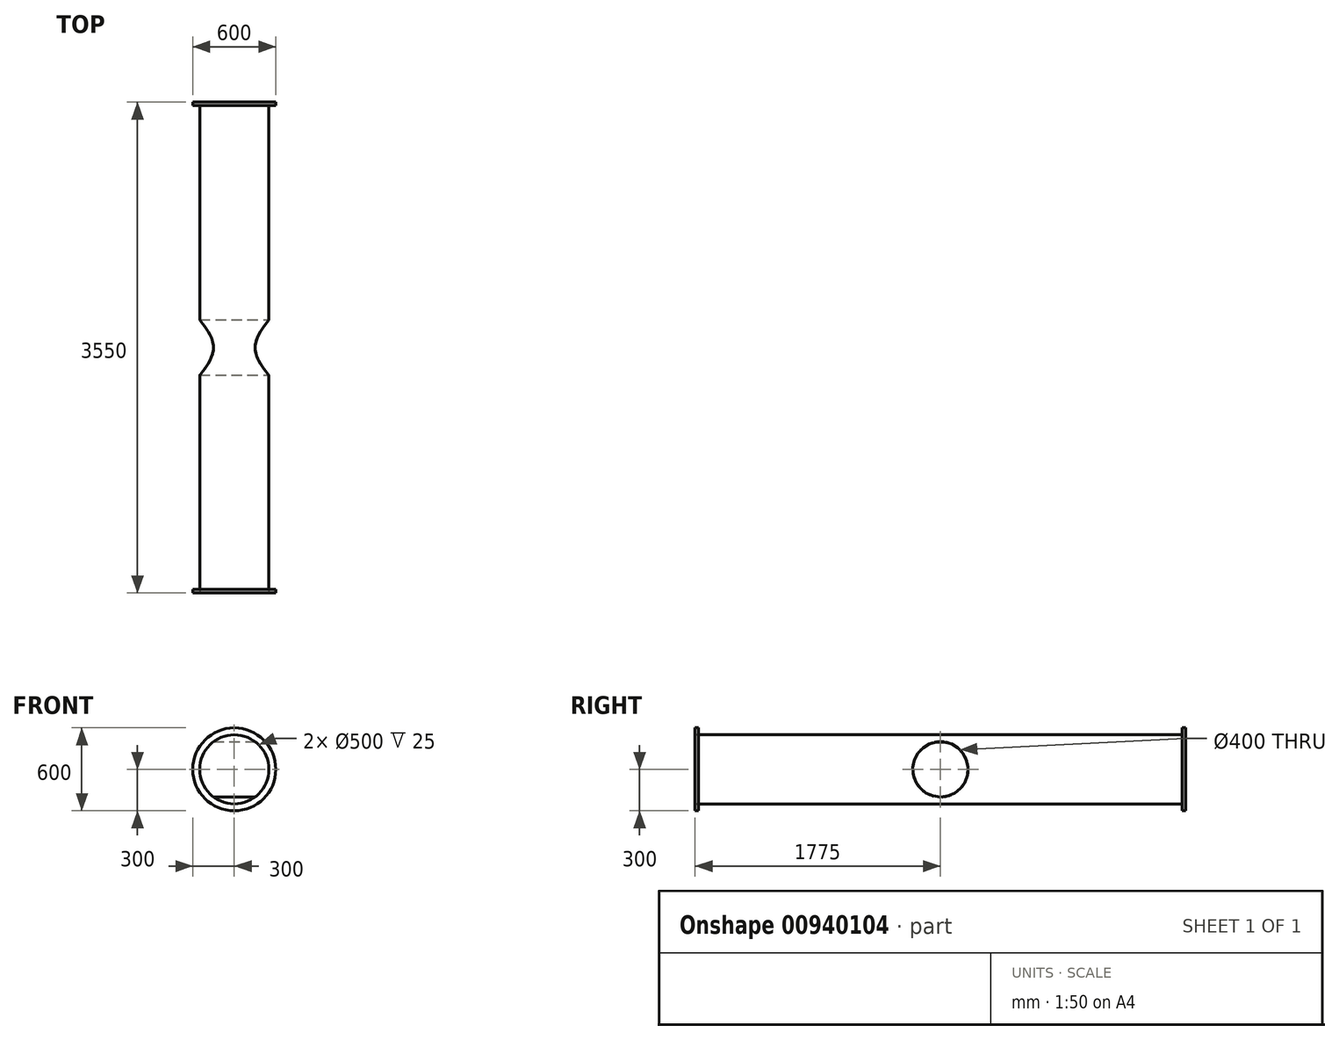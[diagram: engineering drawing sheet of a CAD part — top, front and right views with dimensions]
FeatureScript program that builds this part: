
annotation { "Feature Type Name" : "Feature", "Feature Type Description" : "" }
export const myFeature = defineFeature(function(context is Context, id is Id, definition is map)
    precondition{}
    {
        {
            var Q0;
            Q0=qCreatedBy(makeId("Front.planeOp"),FACE);
            var sketch = newSketch(context, id + "F0", { "sketchPlane" : qUnion([Q0])});
            skCircle(sketch, "E0", {"center": v(0, 0) * mm, "radius": 250 * mm});
            skSolve(sketch);
        }
        {
            var Q0;
            Q0=makeQuery(id+"F0.imprint","IMPRINT",FACE,{"disambiguationData":[TD([[makeQuery(id+"F0.imprint","IMPRINT",EDGE,{"derivedFrom":sQuery(id+"F0.wireOp",EDGE,"E0")}),1.0]])]});
            extrude(context, id + "F1", {"entities" : qUnion([Q0]), "endBound" : BoundingType.SYMMETRIC, "depth" : 3550 * mm, "offsetDistance" : 25 * mm});
        }
        {
            var Q0;
            Q0=makeQuery(id+"F1.opExtrude","CAP_FACE",FACE,{"disambiguationData":[OSD([sQuery(id+"F0.wireOp",EDGE,"E0")])],"isStart":false});
            var sketch = newSketch(context, id + "F2", { "sketchPlane" : qUnion([Q0])});
            skCircle(sketch, "E1", {"center": v(0, 0) * mm, "radius": 300 * mm});
            skSolve(sketch);
        }
        {
            var Q0;
            Q0=makeQuery(id+"F2.imprint","IMPRINT",FACE,{"disambiguationData":[TD([[makeQuery(id+"F2.imprint","IMPRINT",EDGE,{"derivedFrom":sQuery(id+"F2.wireOp",EDGE,"E1")}),1.0]])]});
            extrude(context, id + "F3", {"entities" : qUnion([Q0]), "oppositeDirection" : true, "depth" : 25 * mm, "offsetDistance" : 25 * mm});
        }
        {
            var Q0;
            Q0=makeQuery(id+"F1.opExtrude","CAP_FACE",FACE,{"disambiguationData":[OSD([sQuery(id+"F0.wireOp",EDGE,"E0")])],"isStart":true});
            var sketch = newSketch(context, id + "F4", { "sketchPlane" : qUnion([Q0])});
            skCircle(sketch, "E2", {"center": v(0, 0) * mm, "radius": 300 * mm});
            skSolve(sketch);
        }
        {
            var Q0;
            Q0=makeQuery(id+"F4.imprint","IMPRINT",FACE,{"disambiguationData":[TD([[makeQuery(id+"F4.imprint","IMPRINT",EDGE,{"derivedFrom":sQuery(id+"F4.wireOp",EDGE,"E2")}),1.0]])]});
            extrude(context, id + "F5", {"entities" : qUnion([Q0]), "operationType" : NewBodyOperationType.ADD, "oppositeDirection" : true, "depth" : 25 * mm, "offsetDistance" : 25 * mm});
        }
        {
            var Q0;
            Q0=qCreatedBy(makeId("Right.planeOp"),FACE);
            var sketch = newSketch(context, id + "F6", { "sketchPlane" : qUnion([Q0])});
            skCircle(sketch, "E3", {"center": v(0, 0) * mm, "radius": 200 * mm});
            skSolve(sketch);
        }
        {
            var Q0;
            Q0 = qSketchRegion(id + "F6", true);
            extrude(context, id + "F7", {"entities" : qUnion([Q0]), "operationType" : NewBodyOperationType.REMOVE, "endBound" : BoundingType.SYMMETRIC, "oppositeDirection" : true, "depth" : 2466 * mm, "offsetDistance" : 25 * mm});
        }
    });
